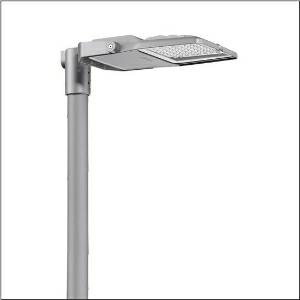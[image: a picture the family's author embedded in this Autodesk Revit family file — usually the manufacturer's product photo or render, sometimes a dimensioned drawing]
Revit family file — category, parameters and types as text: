
# Revit family: floodlight_fl_21_mini___pl64_5xa7775c2e3a_8880
name_source: partatom
category: Lighting Fixtures
units: mm (PartAtom-declared; Revit-internal decimal feet)

## family parameters
Cut with Voids When Loaded = No
Host = Face
Light Source = No
Part Type = Normal
Room Calculation Point = No
Round Connector Dimension = Use Diameter
Shared = No

## types (1)
- --- (1 x LED, 11770 lm, 89 W, 3000K)
    Apparent Load = 89 VA
    CIE Flux Codes = 28 80 98 100 100
    Color Rendering = 70
    Color Temperature = 3000K
    Default Elevation = 1800 mm
    Description = Floodlight FL 21 mini, floodlight, primary light control with lens, of PMMA, primary optical cover: protective disc, of toughened safety glass, transparent, light distribution: PL64, light emission: direct distribution, installation type: surface-mounted, LED, High Power LED, rated luminous flux: 11.770lm, luminous efficacy: 132lm/W, light colour: 730, colour temperature: 3000K, control gear: ECG Smart Interface, control: flexible luminous flux parameterisation, time-dependent luminous flux control, constant luminous flux control, overheat protection, presetting dimming logarithmic, with terminal, 6-pole, mains connection: 220..240V, AC, 50/60Hz, start of lifetime: 89W, end of lifetime: 94W, reduction: 43W, luminaire housing, of diecast aluminium, powder-coated, Siteco® metallic grey (DB 702S), corrosivity category C5 according to DIN EN ISO 12944, mast bracket, of steel, galvanised, powder-coated, Siteco® metallic grey (DB 702S), protection rating (complete): IP66, insulation class (complete): insulation class II (safety insulation), certification: CE, ENEC, VDE, protection symbol: D, impact resistance: IK08, permissible operating ambient temperature: -40..+40°C, permissible operating ambient temperature for outdoor applications: -40..+50°C, standard: DIN EN 12944, packaging unit: 1 piece

Light Distribution: PL64
    Height = 70 mm
    Lamp = 1 x LED
    Lamp Light Flux = 11770 lm
    Lamp Power = 89 W
    Lamp count = 1
    Length = 485 mm
    Luminous efficacy = 132 lm/W
    Manufacturer = Siteco
    ModVariant = No
    Model = 5XA7775C2E3A
    Number of Poles = 1
    OnlyDefault = Yes
    Power Factor = 1
    Product Name = Floodlight FL 21 mini | PL64
    Product group = floodlight | pylon top
    ProductGroupID = 6101
    Protection Class = Protection class II
    Protection Degree = IP 66
    RLX_Detail_Level = 1
    RlxData = <blob elided: 100813 chars, md5=6b32792a>
    Socket = socket
    Standby Power = 0 W
    System Light Flux = 11770 lm
    System Power = 89 W
    Type Comments = factory setting: luminous flux: 100 % | dim-lin: 254 | 456 mA
    Type Image = l_1007125.jpg
    URL = http://relux.com
    VarID = @adj_076531
    Voltage = 0 V
    Weight = 0.00 kg
    Width = 337 mm

## geometry (parser evidence)
native form markers: Blend x4, Sweep x12
no freeform markers — native parametric forms only
